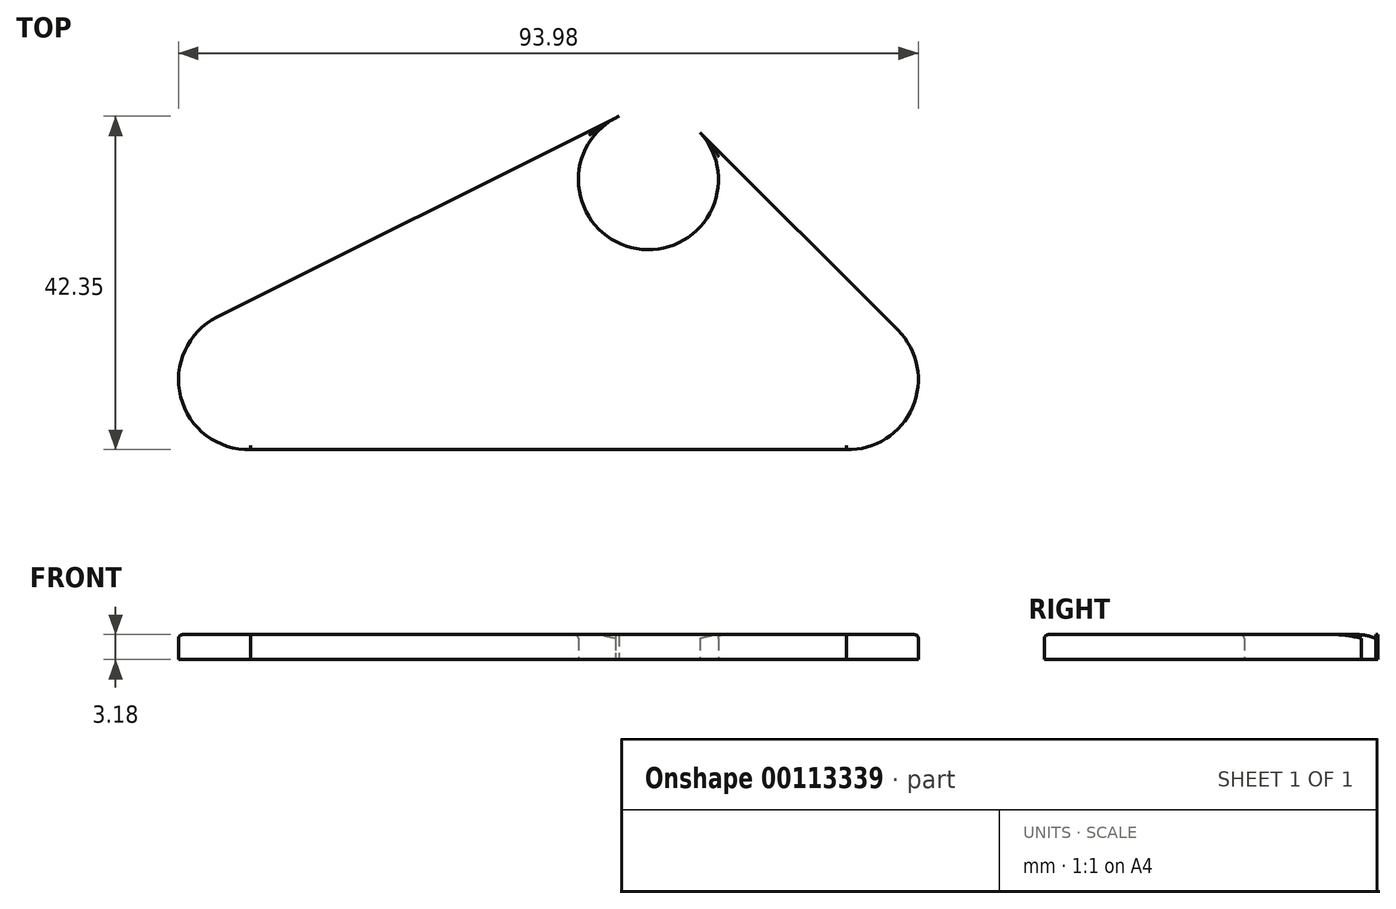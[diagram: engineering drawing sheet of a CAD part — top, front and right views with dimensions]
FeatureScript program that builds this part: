
annotation { "Feature Type Name" : "Feature", "Feature Type Description" : "" }
export const myFeature = defineFeature(function(context is Context, id is Id, definition is map)
    precondition{}
    {
        {
            var Q0;
            Q0=qCreatedBy(makeId("Top.planeOp"),FACE);
            var sketch = newSketch(context, id + "F0", { "sketchPlane" : qUnion([Q0])});
            skCircle(sketch, "E0", {"center": v(0, 0) * mm, "radius": 8.9 * mm});
            skCircle(sketch, "E1", {"center": v(76.2, 0) * mm, "radius": 8.9 * mm});
            skCircle(sketch, "E2", {"center": v(50.8, 25.4) * mm, "radius": 8.9 * mm});
            skLineSegment(sketch, "E3", {"start": v(47.04, 33.46) * mm, "end": v(-3.98, 7.95) * mm});
            skLineSegment(sketch, "E4", {"start": v(0.27, -8.89) * mm, "end": v(75.93, -8.89) * mm});
            skLineSegment(sketch, "E5", {"start": v(56.8, 31.96) * mm, "end": v(82.48, 6.29) * mm});
            skSolve(sketch);
        }
        {
            var Q0;
            {var subQ5=sQuery(id+"F0.wireOp",EDGE,"E4");Q0=makeQuery(id+"F0.imprint","IMPRINT",FACE,{"disambiguationData":[TD([[makeQuery(id+"F0.imprint","IMPRINT",EDGE,{"derivedFrom":subQ5}),1.0]])]});}
            var Q1;
            {var subQ0=sQuery(id+"F0.wireOp",EDGE,"E0");var subQ1=makeQuery(id+"F0.imprint","INTERSECT",VERTEX,{"derivedFrom":[subQ0,sQuery(id+"F0.wireOp",EDGE,"E3")]});Q1=makeQuery(id+"F0.imprint","IMPRINT",FACE,{"disambiguationData":[TD([[makeQuery(id+"F0.imprint","IMPRINT",EDGE,{"disambiguationData":[TD([[subQ1,-1.0]])],"derivedFrom":subQ0}),1.0]])]});}
            var Q2;
            {var subQ0=sQuery(id+"F0.wireOp",EDGE,"E3");var subQ1=sQuery(id+"F0.wireOp",EDGE,"E2");var subQ2=makeQuery(id+"F0.imprint","INTERSECT",VERTEX,{"disambiguationData":[OD(0.0)],"derivedFrom":[subQ1,subQ0]});Q2=makeQuery(id+"F0.imprint","IMPRINT",FACE,{"disambiguationData":[TD([[makeQuery(id+"F0.imprint","IMPRINT",EDGE,{"disambiguationData":[TD([[subQ2,1.0]])],"derivedFrom":subQ1}),1.0]])]});}
            var Q3;
            {var subQ0=sQuery(id+"F0.wireOp",EDGE,"E1");var subQ1=makeQuery(id+"F0.imprint","INTERSECT",VERTEX,{"derivedFrom":[subQ0,sQuery(id+"F0.wireOp",EDGE,"E4")]});Q3=makeQuery(id+"F0.imprint","IMPRINT",FACE,{"disambiguationData":[TD([[makeQuery(id+"F0.imprint","IMPRINT",EDGE,{"disambiguationData":[TD([[subQ1,1.0]])],"derivedFrom":subQ0}),1.0]])]});}
            extrude(context, id + "F1", {"entities" : qUnion([Q0, Q1, Q2, Q3]), "depth" : 3.17 * mm});
        }
        {
            var Q0;
            Q0=makeQuery(id+"F1.opExtrude","CAP_FACE",FACE,{"disambiguationData":[OSD([sQuery(id+"F0.wireOp",EDGE,"E0"),sQuery(id+"F0.wireOp",EDGE,"E1"),sQuery(id+"F0.wireOp",EDGE,"E2"),sQuery(id+"F0.wireOp",EDGE,"E3"),sQuery(id+"F0.wireOp",EDGE,"E4"),sQuery(id+"F0.wireOp",EDGE,"E5")])],"isStart":false});
            fillet(context, id + "F2", {"entities" : qUnion([Q0]), "radius" : 0.5 * mm, "tangentPropagation" : true, "allowEdgeOverflow" : false});
        }
    });
